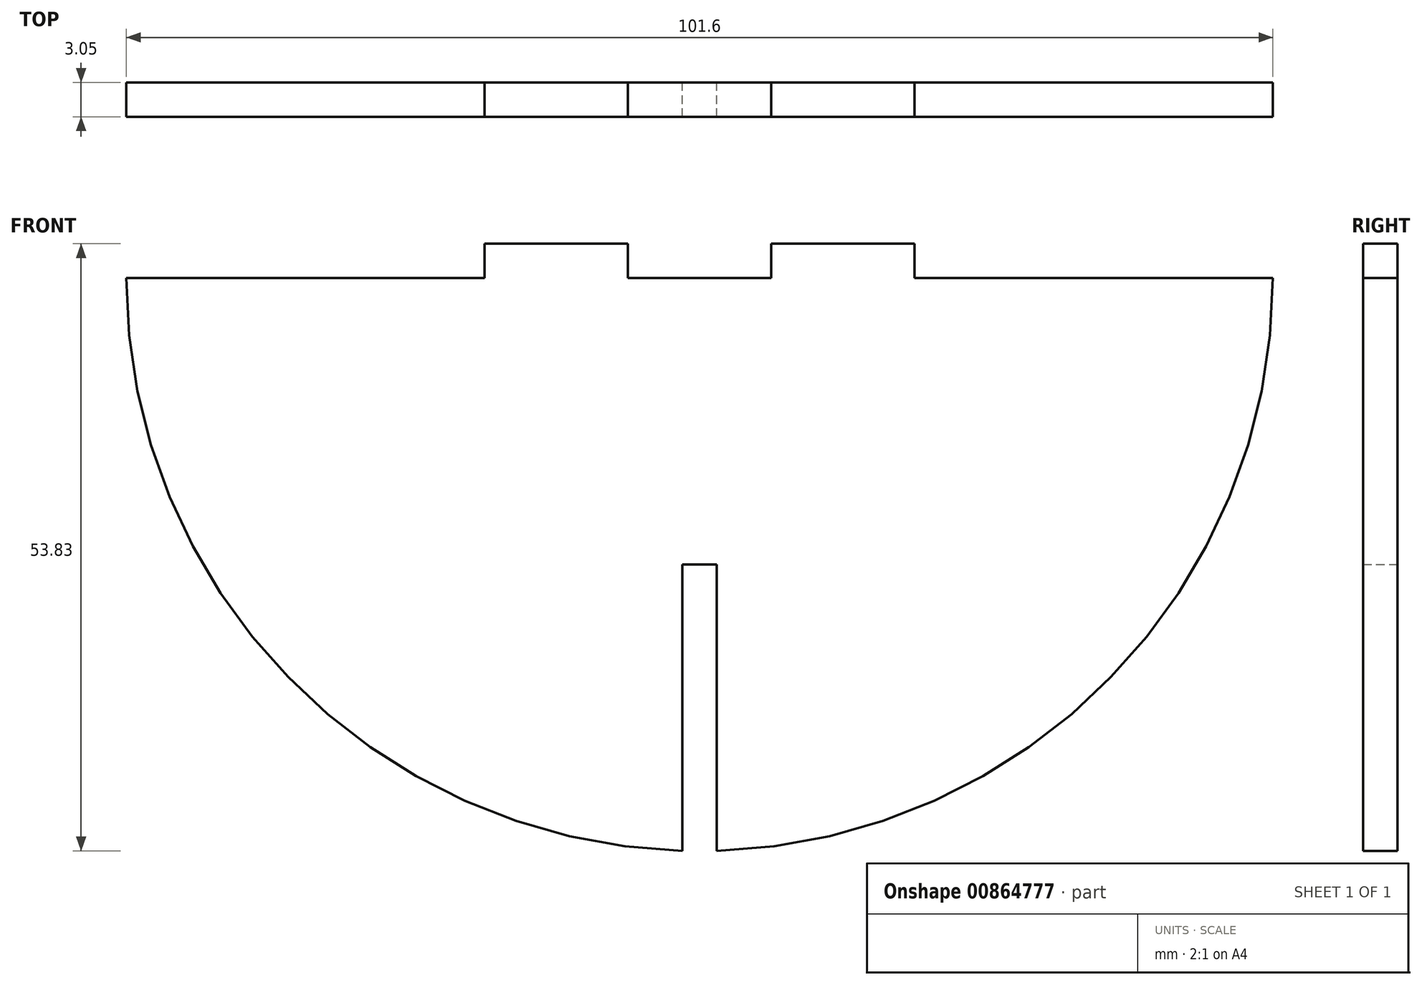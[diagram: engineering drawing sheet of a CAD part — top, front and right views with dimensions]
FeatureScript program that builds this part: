
annotation { "Feature Type Name" : "Feature", "Feature Type Description" : "" }
export const myFeature = defineFeature(function(context is Context, id is Id, definition is map)
    precondition{}
    {
        {
            var Q0;
            Q0=qCreatedBy(makeId("Front.planeOp"),FACE);
            var sketch = newSketch(context, id + "F0", { "sketchPlane" : qUnion([Q0])});
            skArc(sketch, "E0", {"start": v(-50.8, 50.8) * mm, "mid": v(-36.46, 15.42) * mm, "end": v(-1.52, 0.02) * mm});
            skLineSegment(sketch, "E1", {"start": v(-50.8, 50.8) * mm, "end": v(50.8, 50.8) * mm, "construction": true});
            skLineSegment(sketch, "E2", {"start": v(-19.05, 53.85) * mm, "end": v(-6.35, 53.85) * mm});
            skLineSegment(sketch, "E3", {"start": v(-19.05, 53.85) * mm, "end": v(-19.05, 50.8) * mm});
            skLineSegment(sketch, "E4", {"start": v(-19.05, 50.8) * mm, "end": v(-50.8, 50.8) * mm});
            skLineSegment(sketch, "E5", {"start": v(19.05, 53.85) * mm, "end": v(19.05, 50.8) * mm});
            skLineSegment(sketch, "E6", {"start": v(19.05, 50.8) * mm, "end": v(50.8, 50.8) * mm});
            skLineSegment(sketch, "E7", {"start": v(-6.35, 53.85) * mm, "end": v(-6.35, 50.8) * mm});
            skLineSegment(sketch, "E8", {"start": v(-6.35, 50.8) * mm, "end": v(6.35, 50.8) * mm});
            skLineSegment(sketch, "E9", {"start": v(6.35, 50.8) * mm, "end": v(6.35, 53.85) * mm});
            skLineSegment(sketch, "E10.trimOffspring", {"start": v(6.35, 53.85) * mm, "end": v(19.05, 53.85) * mm});
            skLineSegment(sketch, "E11", {"start": v(-1.52, 25.4) * mm, "end": v(1.52, 25.4) * mm});
            skLineSegment(sketch, "E12", {"start": v(1.52, 25.4) * mm, "end": v(1.52, 0.02) * mm});
            skLineSegment(sketch, "E13", {"start": v(-1.52, 25.4) * mm, "end": v(-1.52, 0.02) * mm});
            skArc(sketch, "E14.trimOffspring", {"start": v(1.52, 0.02) * mm, "mid": v(36.46, 15.42) * mm, "end": v(50.8, 50.8) * mm});
            skSolve(sketch);
        }
        {
            var Q0;
            Q0 = qSketchRegion(id + "F0", true);
            extrude(context, id + "F1", {"entities" : qUnion([Q0]), "depth" : 3.05 * mm, "offsetDistance" : 25.4 * mm});
        }
    });
